# Revit family: M_Ceiling Light - Flat Round
name_source: partatom
category: Lighting Fixtures
revit_build: Autodesk Revit 2017 (Build: 20160225_1515(x64)
units: mm (PartAtom-declared; Revit-internal decimal feet)

## family parameters
Cut with Voids When Loaded = No
Host = Face
Light Source = Yes
OmniClass Number = 23.80.70.11.11
OmniClass Title = General Luminaries, Non Directional
Part Type = Normal
Room Calculation Point = No
Round Connector Dimension = Use Diameter
Shared = No

## types (4) — shared parameters
Assembly Code = D5020220
Ballast Number of Poles = 1
Color Filter = 16777215
Default Elevation = 1200 mm
Diffuser Material = Glass, White, High Luminance
Dimming Lamp Color Temperature Shift = <None>
Emit Shape Visible in Rendering = No
Emit from Circle Diameter = 254 mm
Light Box Material = Steel, Paint Finish, Dark Gray, Matte
Load Classification = Lighting - Dwelling Unit
Tilt Angle = -90.00°

## per-type parameters (varying)
| type | Apparent Load | Ballast Voltage | Lamp | Photometric Web File |
| 60W - 120V | 60 VA | 120 V | A-19 | CLFR1A19.ies |
| 60W - 277V | 60 VA | 277 V | A-19 | CLFR1A19.ies |
| 100W - 120V | 100 VA | 120 V | A-19 | CLFR1A21.ies |
| 100W - 277V | 100 VA | 277 V | A-21 | CLFR1A21.ies |

## geometry (parser evidence)
native form markers: Sweep x3
no freeform markers — native parametric forms only
